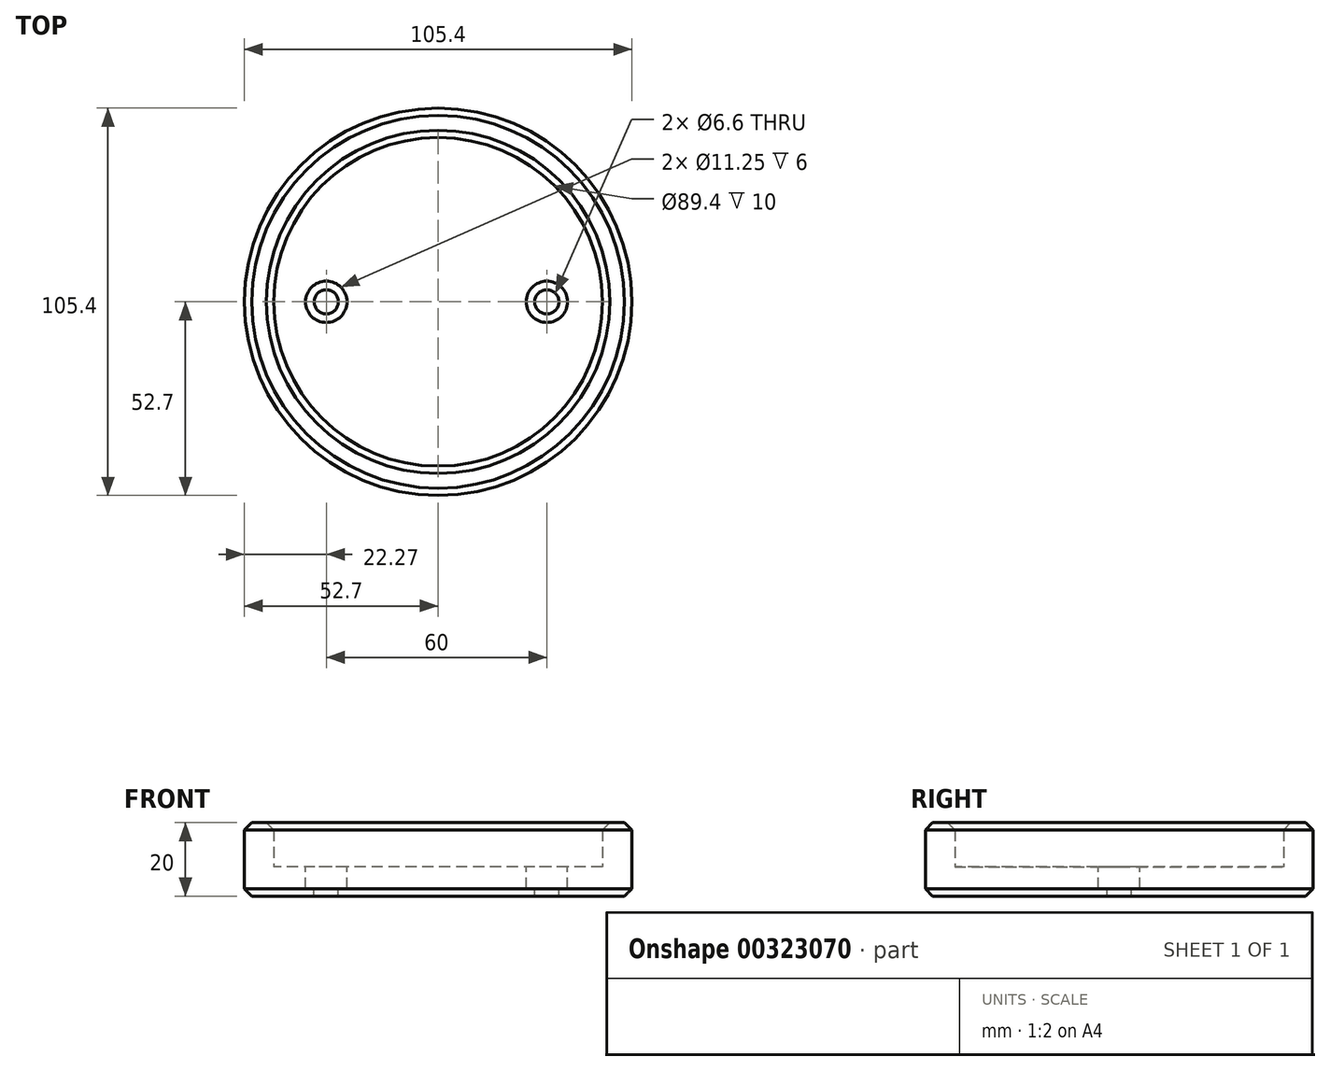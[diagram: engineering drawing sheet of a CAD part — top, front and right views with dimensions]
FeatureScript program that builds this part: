
annotation { "Feature Type Name" : "Feature", "Feature Type Description" : "" }
export const myFeature = defineFeature(function(context is Context, id is Id, definition is map)
    precondition{}
    {
        {
            var Q0;
            Q0=qCreatedBy(makeId("Top.planeOp"),FACE);
            var sketch = newSketch(context, id + "F0", { "sketchPlane" : qUnion([Q0])});
            skCircle(sketch, "E0", {"center": v(0, 0) * mm, "radius": 44.7 * mm});
            skCircle(sketch, "E1.0", {"center": v(0, 0) * mm, "radius": 52.7 * mm});
            skSolve(sketch);
        }
        {
            var Q0;
            Q0=makeQuery(id+"F0.imprint","IMPRINT",FACE,{"disambiguationData":[TD([[makeQuery(id+"F0.imprint","IMPRINT",EDGE,{"derivedFrom":sQuery(id+"F0.wireOp",EDGE,"E0")}),1.0]])]});
            extrude(context, id + "F1", {"entities" : qUnion([Q0]), "depth" : 8 * mm});
        }
        {
            var Q0;
            Q0=makeQuery(id+"F0.imprint","IMPRINT",FACE,{"disambiguationData":[TD([[makeQuery(id+"F0.imprint","IMPRINT",EDGE,{"derivedFrom":sQuery(id+"F0.wireOp",EDGE,"E0")}),-1.0]])]});
            extrude(context, id + "F2", {"entities" : qUnion([Q0]), "operationType" : NewBodyOperationType.ADD, "depth" : 20 * mm});
        }
        {
            var Q0;
            Q0=makeQuery(id+"F1.opExtrude","CAP_FACE",FACE,{"disambiguationData":[OSD([sQuery(id+"F0.wireOp",EDGE,"E0")])],"isStart":false});
            var sketch = newSketch(context, id + "F3", { "sketchPlane" : qUnion([Q0])});
            skPoint(sketch, "E2", {"position": v(-30.43, 0) * mm});
            skPoint(sketch, "E3", {"position": v(29.57, 0) * mm});
            skSolve(sketch);
        }
        {
            var Q0;
            Q0=sQuery(id+"F3.wireOp",VERTEX,"E2");
            var Q1;
            Q1=sQuery(id+"F3.wireOp",VERTEX,"E3");
            var Q2;
            Q2=makeQuery(id+"F1.opExtrude","SWEPT_BODY",BODY,{"disambiguationData":[OSD([sQuery(id+"F0.wireOp",EDGE,"E0")])]});
            hole(context, id + "F4", {"style" : HoleStyle.C_BORE, "endStyle" : HoleEndStyle.THROUGH, "standardTappedOrClearance" : lookupTablePath({ "standard" : "ISO", "fit" : "Normal", "size" : "M6", "type" : "Clearance" }), "standardBlindInLast" : lookupTablePath({ "fit" : "Standard", "standard" : "ISO", "size" : "M6", "type" : "Clearance" }), "holeDiameter" : 6.6 * mm, "cBoreDiameter" : 11.25 * mm, "cBoreDepth" : 6 * mm, "tappedDepth" : 12 * mm, "tapClearance" : 3, "locations" : qUnion([Q0, Q1]), "scope" : qUnion([Q2])});
        }
        {
            var Q0;
            Q0=makeQuery(id+"F2.opExtrude","CAP_EDGE",EDGE,{"disambiguationData":[OSD([sQuery(id+"F0.wireOp",EDGE,"E1.0")])],"isStart":true});
            var Q1;
            Q1=makeQuery(id+"F2.opExtrude","CAP_EDGE",EDGE,{"disambiguationData":[OSD([sQuery(id+"F0.wireOp",EDGE,"E1.0")])],"isStart":false});
            var Q2;
            Q2=makeQuery(id+"F2.opExtrude","CAP_EDGE",EDGE,{"disambiguationData":[OSD([sQuery(id+"F0.wireOp",EDGE,"E0")])],"isStart":false});
            chamfer(context, id + "F5", {"entities" : qUnion([Q0, Q1, Q2]), "width" : 2 * mm, "tangentPropagation" : true});
        }
    });
